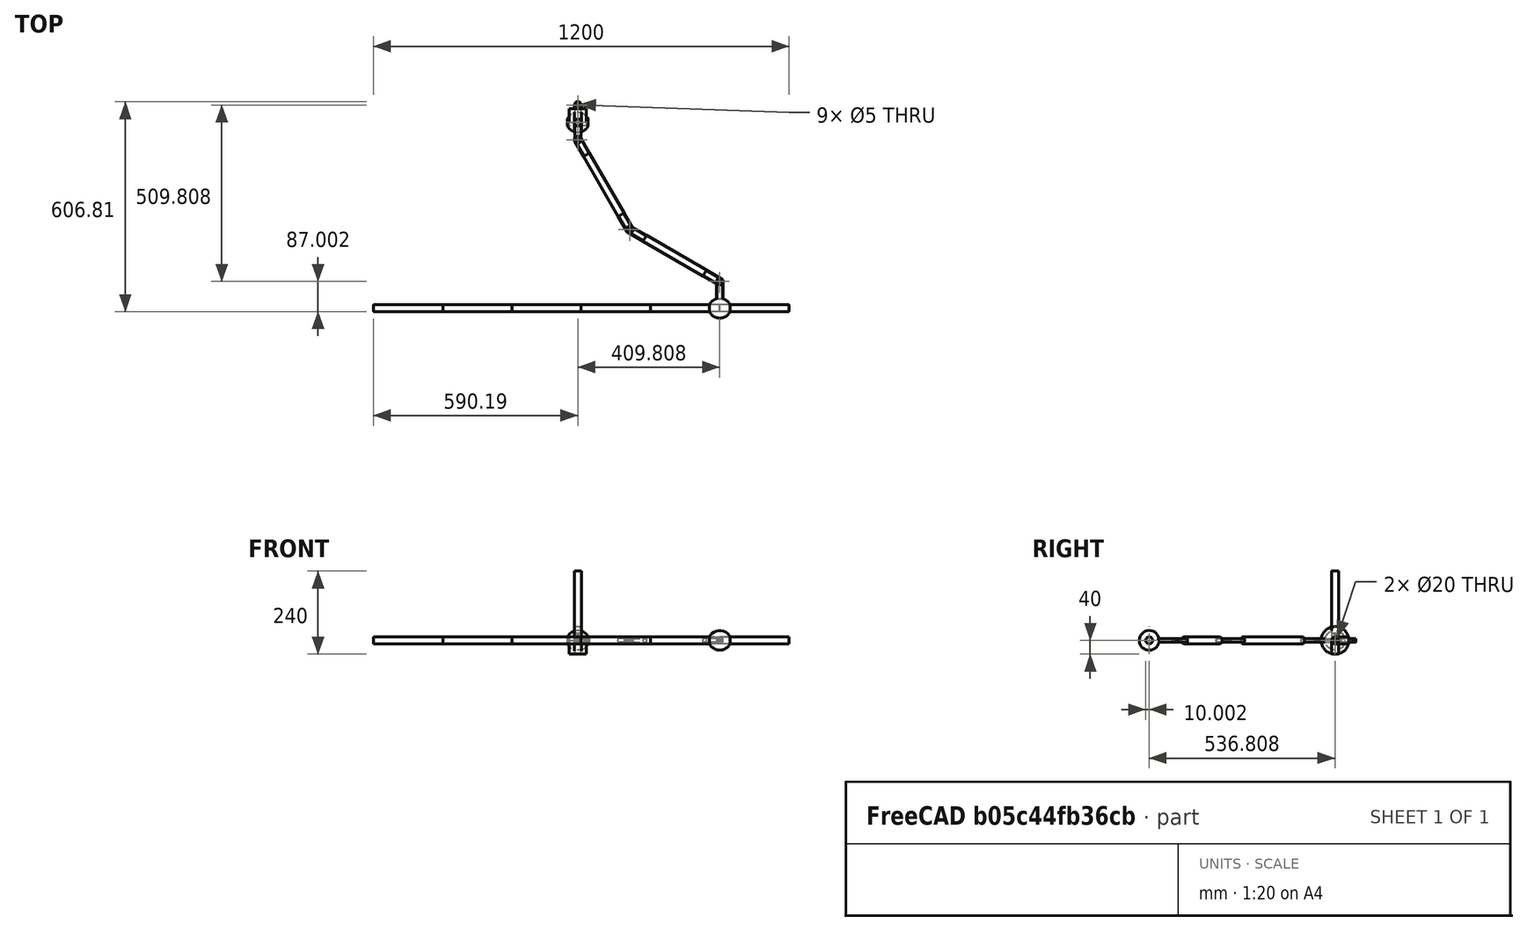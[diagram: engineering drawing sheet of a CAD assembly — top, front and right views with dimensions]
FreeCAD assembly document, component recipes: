
FREECAD ASSEMBLY — COMPONENT RECIPES ("Demo6RevRev")

This assembly document has 7 components, labeled P0..P6 below (a component is one placed body or linked part). 7 of them carry a construction recipe — the FreeCAD feature program that regenerates the part from scratch, quoted from this document or its linked companion documents; the rest are supplied as boundary geometry only. No exploded tour is included for this assembly.
COMPONENT P0 — recipe-attached ("Weight", modeled in this document).
Construction recipe (the document's own serialized feature program — sketch geometry with constraints, then the solid features built on it; lengths are millimeters unless a unit is written):

FEATURE [Sketcher::SketchObject] Sketch
  FullyConstrained = true
  MapMode = 5
  Support = -> [XY_Plane]
  sketch-geometry (2):
    g0: LineSegment StartX=-30 StartY=10 StartZ=0 EndX=30 EndY=10 EndZ=0
    g1: ArcOfCircle CenterX=0 CenterY=-5 CenterZ=0 NormalX=0 NormalY=0 NormalZ=1 AngleXU=0 Radius=33.541 StartAngle=0.463648 EndAngle=2.67795
  constraints (7):
    c: Horizontal(g0)
    c: DistanceY(g-1,g0) = 10
    c: DistanceX(g-1,g0) = 30
    c: PointOnObject(g1,g-2)
    c: DistanceY(g1,g-1) = 5
    c: Coincident(g1,g0)
    c: Coincident(g1,g0)
FEATURE [PartDesign::Revolution] Revolution
  Angle = 360
  Axis = (1,0,0)
  Base = (0,0,0)
  Profile = -> Sketch
  ReferenceAxis = -> Sketch [H_Axis]
FEATURE [PartDesign::CoordinateSystem] WeightTop
  AttacherType = Attacher::AttachEngine3D
  MapMode = 11
  Placement = pos=(30,-1.8e-15,0) rot=(0.707107,0,0.707107;3.14159rad)
  Support = -> [Revolution]
FEATURE [PartDesign::CoordinateSystem] WeightBot
  AttacherType = Attacher::AttachEngine3D
  MapMode = 11
  Placement = pos=(-30,0,0) rot=(0.707107,0,0.707107;3.14159rad)
  Support = -> [Revolution]
FEATURE [PartDesign::CoordinateSystem] WeightLCS
  AttacherType = Attacher::AttachEngine3D
  MapMode = 2
  Support = -> [Body003]
FEATURE [PartDesign::Body] Body  label="Weight"
  Group = -> [Sketch,Revolution,WeightLCS,WeightTop,WeightBot]
  Origin = -> Origin
  Tip = -> Revolution
COMPONENT P1 — recipe-attached ("Rod", modeled in this document).
Construction recipe (the document's own serialized feature program — sketch geometry with constraints, then the solid features built on it; lengths are millimeters unless a unit is written):

FEATURE [Sketcher::SketchObject] Sketch001
  FullyConstrained = true
  MapMode = 5
  Support = -> [XY_Plane001]
  sketch-geometry (1):
    g0: Circle CenterX=0 CenterY=0 CenterZ=0 NormalX=0 NormalY=0 NormalZ=1 AngleXU=0 Radius=10
  constraints (2):
    c: Coincident(g0,g-1)
    c: Diameter(g0) = 20
FEATURE [PartDesign::Pad] Pad
  Direction = (0,0,1)
  Length = 200
  Length2 = 10
  Profile = -> Sketch001
  ReferenceAxis = -> Sketch001 [N_Axis]
  Type = 0
FEATURE [PartDesign::CoordinateSystem] RodTop
  AttacherType = Attacher::AttachEngine3D
  MapMode = 11
  Placement = pos=(0,0,200) rot=(0,0,1;1.5708rad)
  Support = -> [Pad]
FEATURE [PartDesign::CoordinateSystem] RodBottom
  AttacherType = Attacher::AttachEngine3D
  MapMode = 11
  Placement = pos=(0,0,0) rot=(0,0,1;1.5708rad)
  Support = -> [Pad]
FEATURE [PartDesign::Body] Body001  label="Rod"
  Group = -> [Sketch001,Pad,RodTop,RodBottom]
  Origin = -> Origin001
  Tip = -> Pad
COMPONENT P2 — recipe-attached ("LugBody", modeled in this document).
Construction recipe (the document's own serialized feature program — sketch geometry with constraints, then the solid features built on it; lengths are millimeters unless a unit is written):

FEATURE [Sketcher::SketchObject] Sketch002
  FullyConstrained = true
  MapMode = 5
  Support = -> [XY_Plane002]
  sketch-geometry (5):
    g0: LineSegment StartX=-10 StartY=0 StartZ=0 EndX=-10 EndY=50 EndZ=0
    g1: ArcOfCircle CenterX=0 CenterY=50 CenterZ=0 NormalX=0 NormalY=0 NormalZ=1 AngleXU=0 Radius=10 StartAngle=1e-16 EndAngle=3.14159
    g2: LineSegment StartX=10 StartY=50 StartZ=0 EndX=10 EndY=0 EndZ=0
    g3: LineSegment StartX=10 StartY=0 StartZ=0 EndX=-10 EndY=0 EndZ=0
    g4: Circle CenterX=0 CenterY=50 CenterZ=0 NormalX=0 NormalY=0 NormalZ=1 AngleXU=0 Radius=2.5
  constraints (13):
    c: PointOnObject(g0,g-1)
    c: Vertical(g0)
    c: Tangent(g0,g1) = 1.5708
    c: Tangent(g1,g2) = 1.5708
    c: Coincident(g2,g3)
    c: Coincident(g3,g0)
    c: Horizontal(g3)
    c: PointOnObject(g1,g-2)
    c: Vertical(g2)
    c: Diameter(g1) = 20
    c: Distance(g2) = 50
    c: Coincident(g4,g1)
    c: Diameter(g4) = 5
FEATURE [PartDesign::Pad] Pad001
  Direction = (0,0,1)
  Length = 10
  Length2 = 10
  Midplane = true
  Profile = -> Sketch002
  ReferenceAxis = -> Sketch002 [N_Axis]
  Type = 0
FEATURE [PartDesign::Body] Body002  label="LugBody"
  Group = -> [Sketch002,Pad001]
  Origin = -> Origin002
  Tip = -> Pad001
COMPONENT P3 — recipe-attached ("LugCylinder", modeled in this document).
Construction recipe (the document's own serialized feature program — sketch geometry with constraints, then the solid features built on it; lengths are millimeters unless a unit is written):

FEATURE [Sketcher::SketchObject] Sketch003
  FullyConstrained = true
  MapMode = 5
  Placement = pos=(0,0,0) rot=(1,0,0;1.5708rad)
  Support = -> [XZ_Plane003]
  sketch-geometry (1):
    g0: Circle CenterX=0 CenterY=0 CenterZ=0 NormalX=0 NormalY=0 NormalZ=1 AngleXU=0 Radius=10
  constraints (2):
    c: Coincident(g0,g-1)
    c: Diameter(g0) = 20
FEATURE [PartDesign::Pad] Pad002
  Direction = (0,-1,-2e-16)
  Length = 60
  Length2 = 10
  Placement = pos=(0,0,0) rot=(1,0,0;1.5708rad)
  Profile = -> Sketch003
  ReferenceAxis = -> Sketch003 [N_Axis]
  Reversed = true
  Type = 0
FEATURE [PartDesign::Boolean] Boolean
  BaseFeature = -> Pad002
  Group = -> [Body002]
  Type = 2
FEATURE [PartDesign::CoordinateSystem] LugHole
  AttacherType = Attacher::AttachEngine3D
  MapMode = 11
  Placement = pos=(0,50,5) rot=(0,0,1;1.5708rad)
  Support = -> [Boolean]
FEATURE [PartDesign::CoordinateSystem] LugFace
  AttacherType = Attacher::AttachEngine3D
  MapMode = 5
  Placement = pos=(0,0,0) rot=(1,0,0;1.5708rad)
  Support = -> [Boolean]
FEATURE [PartDesign::CoordinateSystem] LugRot30
  AttacherType = Attacher::AttachEngine3D
  AttachmentOffset = pos=(0,0,0) rot=(0,0,1;0.523599rad)
  MapMode = 11
  Placement = pos=(0,50,5) rot=(0,0,1;2.0944rad)
  Support = -> [Boolean]
FEATURE [PartDesign::CoordinateSystem] LugRot60
  AttacherType = Attacher::AttachEngine3D
  AttachmentOffset = pos=(0,0,0) rot=(0,0,1;1.0472rad)
  MapMode = 11
  Placement = pos=(0,50,5) rot=(0,0,1;2.61799rad)
  Support = -> [Boolean]
FEATURE [PartDesign::Body] Body003  label="LugCylinder"
  Group = -> [Sketch003,Pad002,Boolean,LugHole,LugFace,LugRot30,LugRot60]
  Origin = -> Origin003
  Tip = -> Boolean
COMPONENT P4 — recipe-attached ("BobBody", modeled in this document).
Construction recipe (the document's own serialized feature program — sketch geometry with constraints, then the solid features built on it; lengths are millimeters unless a unit is written):

FEATURE [Sketcher::SketchObject] Sketch004
  FullyConstrained = true
  MapMode = 5
  Support = -> [XY_Plane004]
  sketch-geometry (4):
    g0: LineSegment StartX=-10 StartY=0 StartZ=0 EndX=-10 EndY=30 EndZ=0
    g1: ArcOfCircle CenterX=0 CenterY=30 CenterZ=0 NormalX=0 NormalY=0 NormalZ=1 AngleXU=0 Radius=10 StartAngle=2e-16 EndAngle=3.14159
    g2: LineSegment StartX=10 StartY=30 StartZ=0 EndX=10 EndY=0 EndZ=0
    g3: LineSegment StartX=10 StartY=0 StartZ=0 EndX=-10 EndY=0 EndZ=0
  constraints (11):
    c: PointOnObject(g0,g-1)
    c: Vertical(g0)
    c: Tangent(g0,g1) = 1.5708
    c: Tangent(g1,g2) = 1.5708
    c: Coincident(g2,g3)
    c: Coincident(g3,g0)
    c: Vertical(g2)
    c: PointOnObject(g1,g-2)
    c: Diameter(g1) = 20
    c: Distance(g0) = 30
    c: PointOnObject(g2,g-1)
FEATURE [PartDesign::Revolution] Revolution001
  Angle = 360
  Axis = (1,0,0)
  Base = (0,0,0)
  Profile = -> Sketch004
  ReferenceAxis = -> Sketch004 [H_Axis]
FEATURE [PartDesign::CoordinateSystem] BobBody  label="BobBody001"
  AttacherType = Attacher::AttachEngine3D
  MapMode = 11
  Placement = pos=(-10,0,0) rot=(0.707107,0,0.707107;3.14159rad)
  Support = -> [Revolution001]
FEATURE [PartDesign::Body] Body004  label="BobBody"
  Group = -> [Sketch004,Revolution001,BobBody]
  Origin = -> Origin004
  Tip = -> Revolution001
COMPONENT P5 — recipe-attached ("GroundBody", modeled in this document).
Construction recipe (the document's own serialized feature program — sketch geometry with constraints, then the solid features built on it; lengths are millimeters unless a unit is written):

FEATURE [Sketcher::SketchObject] Sketch005
  FullyConstrained = true
  MapMode = 5
  Support = -> [XY_Plane005]
  sketch-geometry (4):
    g0: LineSegment StartX=-25 StartY=10 StartZ=0 EndX=25 EndY=10 EndZ=0
    g1: LineSegment StartX=25 StartY=10 StartZ=0 EndX=25 EndY=-10 EndZ=0
    g2: LineSegment StartX=25 StartY=-10 StartZ=0 EndX=-25 EndY=-10 EndZ=0
    g3: LineSegment StartX=-25 StartY=-10 StartZ=0 EndX=-25 EndY=10 EndZ=0
  constraints (11):
    c: Coincident(g0,g1)
    c: Coincident(g1,g2)
    c: Coincident(g2,g3)
    c: Coincident(g3,g0)
    c: Horizontal(g0)
    c: Horizontal(g2)
    c: Vertical(g1)
    c: Vertical(g3)
    c: DistanceY(g2,g0) = 20
    c: DistanceX(g0,g0) = 50
    c: Symmetric(g0,g1,g-1)
FEATURE [PartDesign::Pad] Pad003
  Direction = (0,0,1)
  Length = 40
  Length2 = 10
  Profile = -> Sketch005
  ReferenceAxis = -> Sketch005 [N_Axis]
  Reversed = true
  Type = 0
FEATURE [PartDesign::CoordinateSystem] GroundLCS
  AttacherType = Attacher::AttachEngine3D
  MapMode = 5
  Placement = pos=(0,0,-40) rot=(1,0,0;3.14159rad)
  Support = -> [Pad003]
FEATURE [PartDesign::Body] Body005  label="GroundBody"
  Group = -> [Sketch005,Pad003,GroundLCS]
  Origin = -> Origin005
  Tip = -> Pad003
COMPONENT P6 — recipe-attached ("Spacer", modeled in this document).
Construction recipe (the document's own serialized feature program — sketch geometry with constraints, then the solid features built on it; lengths are millimeters unless a unit is written):

FEATURE [Sketcher::SketchObject] Sketch006
  FullyConstrained = true
  MapMode = 5
  Support = -> [XY_Plane007]
  sketch-geometry (2):
    g0: Circle CenterX=0 CenterY=0 CenterZ=0 NormalX=0 NormalY=0 NormalZ=1 AngleXU=0 Radius=10
    g1: Circle CenterX=0 CenterY=0 CenterZ=0 NormalX=0 NormalY=0 NormalZ=1 AngleXU=0 Radius=2.5
  constraints (4):
    c: Coincident(g0,g-1)
    c: Coincident(g1,g0)
    c: Diameter(g0) = 20
    c: Diameter(g1) = 5
FEATURE [PartDesign::Pad] Pad004
  Direction = (0,0,1)
  Length = 20
  Length2 = 10
  Profile = -> Sketch006
  ReferenceAxis = -> Sketch006 [N_Axis]
  Type = 0
FEATURE [PartDesign::CoordinateSystem] SpacerTop
  AttacherType = Attacher::AttachEngine3D
  MapMode = 11
  Placement = pos=(0,0,20) rot=(0,0,1;1.5708rad)
  Support = -> [Pad004]
FEATURE [PartDesign::Body] Body006  label="Spacer"
  Group = -> [Sketch006,Pad004,SpacerTop]
  Origin = -> Origin007
  Tip = -> Pad004
PROVENANCE & LICENSES
A FreeCAD (.FCStd) document from a public repository crawl; recipes are the document's own serialized feature recipes (and, for linked parts, companion documents' recipes).
License: gpl-3.0.
